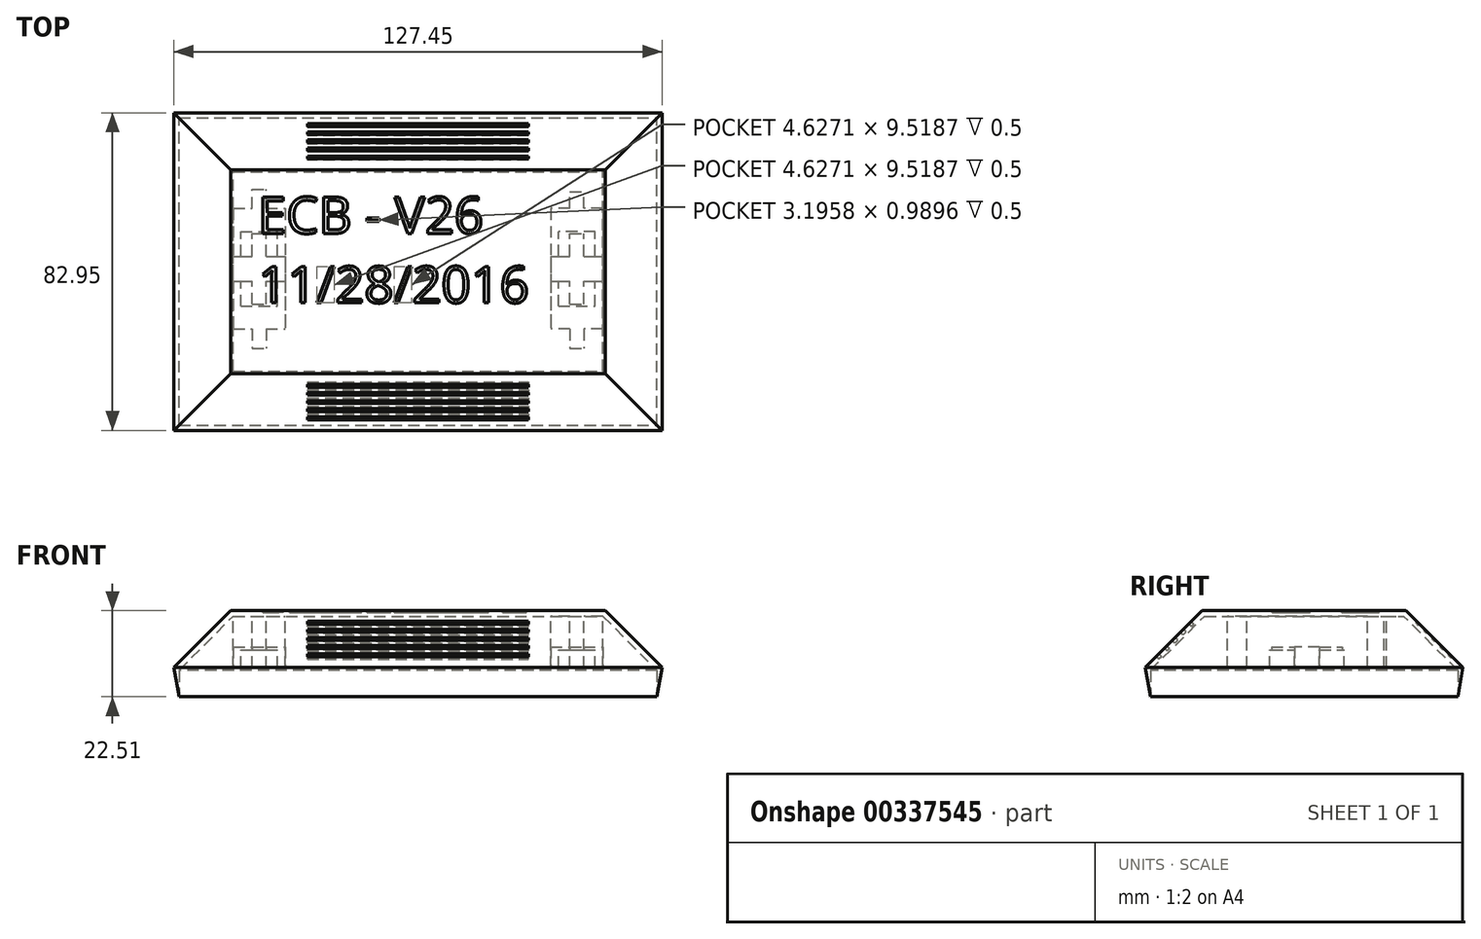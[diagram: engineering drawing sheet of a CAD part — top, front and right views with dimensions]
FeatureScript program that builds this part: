
annotation { "Feature Type Name" : "Feature", "Feature Type Description" : "" }
export const myFeature = defineFeature(function(context is Context, id is Id, definition is map)
    precondition{}
    {
        {
            var Q0;
            Q0=qCreatedBy(makeId("Top.planeOp"),FACE);
            var sketch = newSketch(context, id + "F0", { "sketchPlane" : qUnion([Q0])});
            skLineSegment(sketch, "E0.bottom", {"start": v(0, 0) * mm, "end": v(127.75, 0) * mm});
            skLineSegment(sketch, "E0.top", {"start": v(0, 83.25) * mm, "end": v(127.75, 83.25) * mm});
            skLineSegment(sketch, "E0.left", {"start": v(0, 0) * mm, "end": v(0, 83.25) * mm});
            skLineSegment(sketch, "E0.right", {"start": v(127.75, 0) * mm, "end": v(127.75, 83.25) * mm});
            skLineSegment(sketch, "E1.bottom", {"start": v(0, 0) * mm, "end": v(1.5, 0) * mm});
            skLineSegment(sketch, "E1.left", {"start": v(0, 0) * mm, "end": v(0, 1.5) * mm});
            skLineSegment(sketch, "E2.bottom", {"start": v(127.75, 83.25) * mm, "end": v(126.25, 83.25) * mm});
            skLineSegment(sketch, "E2.left", {"start": v(127.75, 83.25) * mm, "end": v(127.75, 81.75) * mm});
            skSolve(sketch);
        }
        {
            var Q0;
            Q0=makeQuery(id+"F0.imprint","IMPRINT",FACE,{"disambiguationData":[TD([[makeQuery(id+"F0.imprint","IMPRINT",EDGE,{"derivedFrom":sQuery(id+"F0.wireOp",EDGE,"E0.top")}),-1.0]])]});
            var Q1;
            Q1=makeQuery(id+"F0.imprint","IMPRINT",FACE,{"disambiguationData":[TD([[makeQuery(id+"F0.imprint","IMPRINT",EDGE,{"derivedFrom":sQuery(id+"F0.wireOp",EDGE,"E1.bottom")}),1.0]])]});
            var Q2;
            Q2=makeQuery(id+"F0.imprint","IMPRINT",FACE,{"disambiguationData":[TD([[makeQuery(id+"F0.imprint","IMPRINT",EDGE,{"derivedFrom":sQuery(id+"F0.wireOp",EDGE,"E0.bottom")}),1.0]])]});
            var Q3;
            Q3=makeQuery(id+"F0.imprint","IMPRINT",FACE,{"disambiguationData":[TD([[makeQuery(id+"F0.imprint","IMPRINT",EDGE,{"derivedFrom":sQuery(id+"F0.wireOp",EDGE,"E2.bottom")}),1.0]])]});
            extrude(context, id + "F1", {"entities" : qUnion([Q0, Q1, Q2, Q3]), "depth" : 25 * mm});
        }
        {
            var Q0;
            Q0=makeQuery(id+"F1.opExtrude","CAP_EDGE",EDGE,{"disambiguationData":[OSD([sQuery(id+"F0.wireOp",EDGE,"E0.bottom"),sQuery(id+"F0.wireOp",EDGE,"E1.bottom")])],"isStart":false});
            var Q1;
            Q1=makeQuery(id+"F1.opExtrude","CAP_EDGE",EDGE,{"disambiguationData":[OSD([sQuery(id+"F0.wireOp",EDGE,"E0.top"),sQuery(id+"F0.wireOp",EDGE,"E2.bottom")])],"isStart":false});
            var Q2;
            Q2=makeQuery(id+"F1.opExtrude","CAP_EDGE",EDGE,{"disambiguationData":[OSD([sQuery(id+"F0.wireOp",EDGE,"E0.right"),sQuery(id+"F0.wireOp",EDGE,"E2.left")])],"isStart":false});
            var Q3;
            Q3=makeQuery(id+"F1.opExtrude","CAP_EDGE",EDGE,{"disambiguationData":[OSD([sQuery(id+"F0.wireOp",EDGE,"E0.left"),sQuery(id+"F0.wireOp",EDGE,"E1.left")])],"isStart":false});
            chamfer(context, id + "F2", {"entities" : qUnion([Q0, Q1, Q2, Q3]), "width" : 15 * mm, "tangentPropagation" : true});
        }
        {
            var Q0;
            Q0=makeQuery(id+"F1.opExtrude","CAP_FACE",FACE,{"disambiguationData":[OSD([sQuery(id+"F0.wireOp",EDGE,"E0.bottom"),sQuery(id+"F0.wireOp",EDGE,"E0.top"),sQuery(id+"F0.wireOp",EDGE,"E0.left"),sQuery(id+"F0.wireOp",EDGE,"E0.right"),sQuery(id+"F0.wireOp",EDGE,"E1.bottom"),sQuery(id+"F0.wireOp",EDGE,"E1.left"),sQuery(id+"F0.wireOp",EDGE,"E2.bottom"),sQuery(id+"F0.wireOp",EDGE,"E2.left")])],"isStart":true});
            shell(context, id + "F3", {"entities" : qUnion([Q0]), "thickness" : 1.5 * mm});
        }
        {
            var Q0;
            Q0=makeQuery(id+"F1.opExtrude","CAP_EDGE",EDGE,{"disambiguationData":[OSD([sQuery(id+"F0.wireOp",EDGE,"E0.bottom"),sQuery(id+"F0.wireOp",EDGE,"E1.bottom")])],"isStart":true});
            var Q1;
            Q1=makeQuery(id+"F1.opExtrude","CAP_EDGE",EDGE,{"disambiguationData":[OSD([sQuery(id+"F0.wireOp",EDGE,"E0.left"),sQuery(id+"F0.wireOp",EDGE,"E1.left")])],"isStart":true});
            var Q2;
            Q2=makeQuery(id+"F1.opExtrude","CAP_EDGE",EDGE,{"disambiguationData":[OSD([sQuery(id+"F0.wireOp",EDGE,"E0.top"),sQuery(id+"F0.wireOp",EDGE,"E2.bottom")])],"isStart":true});
            var Q3;
            Q3=makeQuery(id+"F1.opExtrude","CAP_EDGE",EDGE,{"disambiguationData":[OSD([sQuery(id+"F0.wireOp",EDGE,"E0.right"),sQuery(id+"F0.wireOp",EDGE,"E2.left")])],"isStart":true});
            chamfer(context, id + "F4", {"entities" : qUnion([Q0, Q1, Q2, Q3]), "chamferType" : ChamferType.OFFSET_ANGLE, "width" : 11 * mm, "oppositeDirection" : false, "angle" : 10 * degree});
        }
        {
            var Q0;
            Q0=makeQuery(id+"F1.opExtrude","CAP_FACE",FACE,{"disambiguationData":[OSD([sQuery(id+"F0.wireOp",EDGE,"E0.bottom"),sQuery(id+"F0.wireOp",EDGE,"E0.top"),sQuery(id+"F0.wireOp",EDGE,"E0.left"),sQuery(id+"F0.wireOp",EDGE,"E0.right"),sQuery(id+"F0.wireOp",EDGE,"E1.bottom"),sQuery(id+"F0.wireOp",EDGE,"E1.left"),sQuery(id+"F0.wireOp",EDGE,"E2.bottom"),sQuery(id+"F0.wireOp",EDGE,"E2.left")])],"isStart":false});
            cPlane(context, id + "F5", {"entities" : qUnion([Q0]), "cplaneType" : CPlaneType.OFFSET, "offset" : 14 * mm, "oppositeDirection" : true, "width" : 150 * mm, "height" : 150 * mm});
        }
        {
            var Q0;
            Q0=makeQuery(id+"F3.opShell","OFFSET_FACE",FACE,{"disambiguationData":[OSD([sQuery(id+"F0.wireOp",EDGE,"E0.bottom"),sQuery(id+"F0.wireOp",EDGE,"E0.top"),sQuery(id+"F0.wireOp",EDGE,"E0.left"),sQuery(id+"F0.wireOp",EDGE,"E0.right"),sQuery(id+"F0.wireOp",EDGE,"E1.bottom"),sQuery(id+"F0.wireOp",EDGE,"E1.left"),sQuery(id+"F0.wireOp",EDGE,"E2.bottom"),sQuery(id+"F0.wireOp",EDGE,"E2.left")])]});
            cPlane(context, id + "F6", {"entities" : qUnion([Q0]), "cplaneType" : CPlaneType.OFFSET, "offset" : 20 * mm, "width" : 150 * mm, "height" : 150 * mm});
        }
        {
            var Q0;
            Q0=makeQuery(id+"F1.opExtrude","CAP_FACE",FACE,{"disambiguationData":[OSD([sQuery(id+"F0.wireOp",EDGE,"E0.bottom"),sQuery(id+"F0.wireOp",EDGE,"E0.top"),sQuery(id+"F0.wireOp",EDGE,"E0.left"),sQuery(id+"F0.wireOp",EDGE,"E0.right"),sQuery(id+"F0.wireOp",EDGE,"E1.bottom"),sQuery(id+"F0.wireOp",EDGE,"E1.left"),sQuery(id+"F0.wireOp",EDGE,"E2.bottom"),sQuery(id+"F0.wireOp",EDGE,"E2.left")])],"isStart":false});
            var sketch = newSketch(context, id + "F7", { "sketchPlane" : qUnion([Q0])});
            skLineSegment(sketch, "E3.bottom", {"start": v(17.62, 32.62) * mm, "end": v(27.22, 32.62) * mm});
            skLineSegment(sketch, "E3.top", {"start": v(17.62, 52.12) * mm, "end": v(27.22, 52.12) * mm});
            skLineSegment(sketch, "E3.left", {"start": v(17.62, 32.62) * mm, "end": v(17.62, 52.12) * mm});
            skLineSegment(sketch, "E3.right", {"start": v(27.22, 32.62) * mm, "end": v(27.22, 52.12) * mm});
            skLineSegment(sketch, "E4", {"start": v(63.87, -44.18) * mm, "end": v(63.87, 54.3) * mm});
            skLineSegment(sketch, "E5.MirrorCS", {"start": v(100.53, 32.62) * mm, "end": v(100.53, 52.12) * mm});
            skLineSegment(sketch, "E6.MirrorCS", {"start": v(110.13, 32.62) * mm, "end": v(100.53, 32.62) * mm});
            skLineSegment(sketch, "E7.MirrorCS", {"start": v(110.13, 32.62) * mm, "end": v(110.13, 52.12) * mm});
            skLineSegment(sketch, "E8.MirrorCS", {"start": v(110.13, 52.12) * mm, "end": v(100.53, 52.12) * mm});
            skLineSegment(sketch, "E9.bottom", {"start": v(15.62, 58.12) * mm, "end": v(29.22, 58.12) * mm});
            skLineSegment(sketch, "E9.top", {"start": v(15.62, 26.62) * mm, "end": v(29.22, 26.62) * mm});
            skLineSegment(sketch, "E9.left", {"start": v(15.62, 58.12) * mm, "end": v(15.62, 26.62) * mm});
            skLineSegment(sketch, "E9.right", {"start": v(29.22, 58.12) * mm, "end": v(29.22, 26.62) * mm});
            skLineSegment(sketch, "E10.MirrorCS", {"start": v(98.53, 58.12) * mm, "end": v(98.53, 26.62) * mm});
            skLineSegment(sketch, "E11.MirrorCS", {"start": v(112.13, 26.62) * mm, "end": v(98.53, 26.62) * mm});
            skLineSegment(sketch, "E12.MirrorCS", {"start": v(112.13, 58.12) * mm, "end": v(112.13, 26.62) * mm});
            skLineSegment(sketch, "E13.MirrorCS", {"start": v(112.13, 58.12) * mm, "end": v(98.53, 58.12) * mm});
            skLineSegment(sketch, "E14.bottom", {"start": v(20.62, 26.62) * mm, "end": v(24.22, 26.62) * mm});
            skLineSegment(sketch, "E14.top", {"start": v(20.62, 21.62) * mm, "end": v(24.22, 21.62) * mm});
            skLineSegment(sketch, "E14.left", {"start": v(20.62, 26.62) * mm, "end": v(20.62, 21.62) * mm});
            skLineSegment(sketch, "E14.right", {"start": v(24.22, 26.62) * mm, "end": v(24.22, 21.62) * mm});
            skLineSegment(sketch, "E15.bottom", {"start": v(20.62, 58.12) * mm, "end": v(24.22, 58.12) * mm});
            skLineSegment(sketch, "E15.top", {"start": v(20.62, 63.12) * mm, "end": v(24.22, 63.12) * mm});
            skLineSegment(sketch, "E15.left", {"start": v(20.62, 58.12) * mm, "end": v(20.62, 63.12) * mm});
            skLineSegment(sketch, "E15.right", {"start": v(24.22, 58.12) * mm, "end": v(24.22, 63.12) * mm});
            skLineSegment(sketch, "E16.bottom", {"start": v(103.53, 26.62) * mm, "end": v(107.13, 26.62) * mm});
            skLineSegment(sketch, "E16.top", {"start": v(103.53, 21.62) * mm, "end": v(107.13, 21.62) * mm});
            skLineSegment(sketch, "E16.left", {"start": v(103.53, 26.62) * mm, "end": v(103.53, 21.62) * mm});
            skLineSegment(sketch, "E16.right", {"start": v(107.13, 26.62) * mm, "end": v(107.13, 21.62) * mm});
            skLineSegment(sketch, "E17.bottom", {"start": v(103.53, 58.12) * mm, "end": v(107.13, 58.12) * mm});
            skLineSegment(sketch, "E17.top", {"start": v(103.53, 62.5) * mm, "end": v(107.13, 62.5) * mm});
            skLineSegment(sketch, "E17.left", {"start": v(103.53, 58.12) * mm, "end": v(103.53, 62.5) * mm});
            skLineSegment(sketch, "E17.right", {"start": v(107.13, 58.12) * mm, "end": v(107.13, 62.5) * mm});
            skSolve(sketch);
        }
        {
            var Q0;
            Q0=qSketchRegion(id+"F7",true);
            extrude(context, id + "F8", {"entities" : qUnion([Q0]), "operationType" : NewBodyOperationType.ADD, "oppositeDirection" : true, "depth" : 15 * mm});
        }
        {
            var Q0;
            {var subQ0=sQuery(id+"F0.wireOp",EDGE,"E1.bottom");var subQ1=sQuery(id+"F0.wireOp",EDGE,"E0.bottom");var subQ2=sQuery(id+"F0.wireOp",EDGE,"E2.bottom");var subQ3=sQuery(id+"F0.wireOp",EDGE,"E0.top");var subQ4=sQuery(id+"F0.wireOp",EDGE,"E1.left");var subQ5=sQuery(id+"F0.wireOp",EDGE,"E0.left");var subQ6=sQuery(id+"F0.wireOp",EDGE,"E2.left");var subQ7=sQuery(id+"F0.wireOp",EDGE,"E0.right");Q0=makeQuery(id+"F8.boolean.opBoolean","SPLIT",FACE,{"disambiguationData":[TD([makeQuery(id+"F8.opExtrude","SWEPT_FACE",FACE,{"disambiguationData":[OSD([sQuery(id+"F7.wireOp",EDGE,"E9.bottom")])]})])],"derivedFrom":makeQuery(id+"F3.opShell","OFFSET_FACE",FACE,{"disambiguationData":[OSD([subQ1,subQ3,subQ5,subQ7,subQ0,subQ4,subQ2,subQ6])]})});}
            cPlane(context, id + "F9", {"entities" : qUnion([Q0]), "cplaneType" : CPlaneType.OFFSET, "offset" : 0 * mm, "width" : 150 * mm, "height" : 150 * mm});
        }
        {
            var Q0;
            Q0=qCreatedBy(id+"F9.planeOp",FACE);
            var sketch = newSketch(context, id + "F10", { "sketchPlane" : qUnion([Q0])});
            skLineSegment(sketch, "E18.bottom", {"start": v(17.62, -32.62) * mm, "end": v(27.22, -32.62) * mm});
            skLineSegment(sketch, "E18.top", {"start": v(17.62, -52.12) * mm, "end": v(27.22, -52.12) * mm});
            skLineSegment(sketch, "E18.left", {"start": v(17.62, -32.62) * mm, "end": v(17.62, -52.12) * mm});
            skLineSegment(sketch, "E18.right", {"start": v(27.22, -32.62) * mm, "end": v(27.22, -52.12) * mm});
            skLineSegment(sketch, "E19.bottom", {"start": v(100.53, -32.62) * mm, "end": v(110.13, -32.62) * mm});
            skLineSegment(sketch, "E19.top", {"start": v(100.53, -52.12) * mm, "end": v(110.13, -52.12) * mm});
            skLineSegment(sketch, "E19.left", {"start": v(100.53, -32.62) * mm, "end": v(100.53, -52.12) * mm});
            skLineSegment(sketch, "E19.right", {"start": v(110.13, -32.62) * mm, "end": v(110.13, -52.12) * mm});
            skSolve(sketch);
        }
        {
            var Q0;
            Q0=qSketchRegion(id+"F10",true);
            extrude(context, id + "F11", {"entities" : qUnion([Q0]), "operationType" : NewBodyOperationType.ADD, "depth" : 8.75 * mm});
        }
        {
            var Q0;
            Q0=makeQuery(id+"F8.opExtrude","CAP_FACE",FACE,{"disambiguationData":[OSD([sQuery(id+"F7.wireOp",EDGE,"E3.bottom"),sQuery(id+"F7.wireOp",EDGE,"E3.top"),sQuery(id+"F7.wireOp",EDGE,"E3.left"),sQuery(id+"F7.wireOp",EDGE,"E3.right"),sQuery(id+"F7.wireOp",EDGE,"E9.bottom"),sQuery(id+"F7.wireOp",EDGE,"E9.top"),sQuery(id+"F7.wireOp",EDGE,"E9.left"),sQuery(id+"F7.wireOp",EDGE,"E9.right")])],"isStart":false});
            cPlane(context, id + "F12", {"entities" : qUnion([Q0]), "cplaneType" : CPlaneType.OFFSET, "offset" : 0 * mm, "width" : 150 * mm, "height" : 150 * mm});
        }
        {
            var Q0;
            Q0=qCreatedBy(id+"F12.planeOp",FACE);
            var sketch = newSketch(context, id + "F13", { "sketchPlane" : qUnion([Q0])});
            skLineSegment(sketch, "E20.bottom", {"start": v(15.62, -45.62) * mm, "end": v(112.13, -45.62) * mm});
            skLineSegment(sketch, "E20.top", {"start": v(15.62, -39.12) * mm, "end": v(112.13, -39.12) * mm});
            skLineSegment(sketch, "E20.left", {"start": v(15.62, -39.12) * mm, "end": v(15.62, -45.62) * mm});
            skLineSegment(sketch, "E20.right", {"start": v(112.13, -39.12) * mm, "end": v(112.13, -45.62) * mm});
            skLineSegment(sketch, "E21.bottom", {"start": v(20.62, -33.12) * mm, "end": v(24.22, -33.12) * mm});
            skLineSegment(sketch, "E21.top", {"start": v(20.62, -51.62) * mm, "end": v(24.22, -51.62) * mm});
            skLineSegment(sketch, "E21.left", {"start": v(20.62, -33.12) * mm, "end": v(20.62, -51.62) * mm});
            skLineSegment(sketch, "E21.right", {"start": v(24.22, -33.12) * mm, "end": v(24.22, -51.62) * mm});
            skLineSegment(sketch, "E22.bottom", {"start": v(103.53, -33.12) * mm, "end": v(107.13, -33.12) * mm});
            skLineSegment(sketch, "E22.top", {"start": v(103.53, -51.62) * mm, "end": v(107.13, -51.62) * mm});
            skLineSegment(sketch, "E22.left", {"start": v(103.53, -33.12) * mm, "end": v(103.53, -51.62) * mm});
            skLineSegment(sketch, "E22.right", {"start": v(107.13, -33.12) * mm, "end": v(107.13, -51.62) * mm});
            skSolve(sketch);
        }
        {
            var Q0;
            Q0=qSketchRegion(id+"F13",true);
            extrude(context, id + "F14", {"entities" : qUnion([Q0]), "operationType" : NewBodyOperationType.REMOVE, "oppositeDirection" : true, "depth" : 5.5 * mm});
        }
        {
            var Q0;
            Q0=makeQuery(id+"F2.opChamfer","BLEND_FACE",FACE,{"disambiguationData":[OSD([sQuery(id+"F0.wireOp",EDGE,"E0.bottom"),sQuery(id+"F0.wireOp",EDGE,"E1.bottom")])]});
            var sketch = newSketch(context, id + "F15", { "sketchPlane" : qUnion([Q0])});
            skLineSegment(sketch, "E23.bottom", {"start": v(35, 21.28) * mm, "end": v(92.75, 21.28) * mm});
            skLineSegment(sketch, "E23.top", {"start": v(35, 20.28) * mm, "end": v(92.75, 20.28) * mm});
            skLineSegment(sketch, "E23.left", {"start": v(35, 21.28) * mm, "end": v(35, 20.28) * mm});
            skLineSegment(sketch, "E23.right", {"start": v(92.75, 21.28) * mm, "end": v(92.75, 20.28) * mm});
            skLineSegment(sketch, "E24.MirrorCS", {"start": v(92.75, 17.28) * mm, "end": v(92.75, 18.28) * mm});
            skLineSegment(sketch, "E25.MirrorCS", {"start": v(35, 17.28) * mm, "end": v(35, 18.28) * mm});
            skLineSegment(sketch, "E26.MirrorCS", {"start": v(35, 17.28) * mm, "end": v(92.75, 17.28) * mm});
            skLineSegment(sketch, "E27.MirrorCS", {"start": v(35, 18.28) * mm, "end": v(92.75, 18.28) * mm});
            skLineSegment(sketch, "E28.MirrorCS", {"start": v(92.75, 15.28) * mm, "end": v(92.75, 14.28) * mm});
            skLineSegment(sketch, "E29.MirrorCS", {"start": v(35, 15.28) * mm, "end": v(35, 14.28) * mm});
            skLineSegment(sketch, "E30.MirrorCS", {"start": v(35, 14.28) * mm, "end": v(92.75, 14.28) * mm});
            skLineSegment(sketch, "E31.MirrorCS", {"start": v(35, 15.28) * mm, "end": v(92.75, 15.28) * mm});
            skLineSegment(sketch, "E32.bottom", {"start": v(35, 24.28) * mm, "end": v(92.75, 24.28) * mm});
            skLineSegment(sketch, "E32.top", {"start": v(35, 23.28) * mm, "end": v(92.75, 23.28) * mm});
            skLineSegment(sketch, "E32.left", {"start": v(35, 24.28) * mm, "end": v(35, 23.28) * mm});
            skLineSegment(sketch, "E32.right", {"start": v(92.75, 24.28) * mm, "end": v(92.75, 23.28) * mm});
            skLineSegment(sketch, "E33.MirrorCS", {"start": v(92.75, 12.28) * mm, "end": v(92.75, 11.28) * mm});
            skLineSegment(sketch, "E34.MirrorCS", {"start": v(35, 12.28) * mm, "end": v(35, 11.28) * mm});
            skLineSegment(sketch, "E35.MirrorCS", {"start": v(35, 11.28) * mm, "end": v(92.75, 11.28) * mm});
            skLineSegment(sketch, "E36.MirrorCS", {"start": v(35, 12.28) * mm, "end": v(92.75, 12.28) * mm});
            skSolve(sketch);
        }
        {
            var Q0;
            Q0 = qSketchRegion(id + "F15", true);
            extrude(context, id + "F16", {"entities" : qUnion([Q0]), "operationType" : NewBodyOperationType.REMOVE, "oppositeDirection" : true, "depth" : 1 * mm, "offsetDistance" : 25 * mm});
        }
        {
            var Q0;
            Q0=makeQuery(id+"F2.opChamfer","BLEND_FACE",FACE,{"disambiguationData":[OSD([sQuery(id+"F0.wireOp",EDGE,"E0.top"),sQuery(id+"F0.wireOp",EDGE,"E2.bottom")])]});
            var sketch = newSketch(context, id + "F17", { "sketchPlane" : qUnion([Q0])});
            skLineSegment(sketch, "E37.bottom", {"start": v(-92.75, -34.58) * mm, "end": v(-35, -34.58) * mm});
            skLineSegment(sketch, "E37.top", {"start": v(-92.75, -35.58) * mm, "end": v(-35, -35.58) * mm});
            skLineSegment(sketch, "E37.left", {"start": v(-92.75, -34.58) * mm, "end": v(-92.75, -35.58) * mm});
            skLineSegment(sketch, "E37.right", {"start": v(-35, -34.58) * mm, "end": v(-35, -35.58) * mm});
            skLineSegment(sketch, "E38.bottom", {"start": v(-92.75, -37.58) * mm, "end": v(-35, -37.58) * mm});
            skLineSegment(sketch, "E38.top", {"start": v(-92.75, -38.58) * mm, "end": v(-35, -38.58) * mm});
            skLineSegment(sketch, "E38.left", {"start": v(-92.75, -37.58) * mm, "end": v(-92.75, -38.58) * mm});
            skLineSegment(sketch, "E38.right", {"start": v(-35, -37.58) * mm, "end": v(-35, -38.58) * mm});
            skLineSegment(sketch, "E39.bottom", {"start": v(-92.75, -40.58) * mm, "end": v(-35, -40.58) * mm});
            skLineSegment(sketch, "E39.top", {"start": v(-92.75, -41.58) * mm, "end": v(-35, -41.58) * mm});
            skLineSegment(sketch, "E39.left", {"start": v(-92.75, -40.58) * mm, "end": v(-92.75, -41.58) * mm});
            skLineSegment(sketch, "E39.right", {"start": v(-35, -40.58) * mm, "end": v(-35, -41.58) * mm});
            skLineSegment(sketch, "E40.bottom", {"start": v(-92.75, -43.58) * mm, "end": v(-35, -43.58) * mm});
            skLineSegment(sketch, "E40.top", {"start": v(-92.75, -44.58) * mm, "end": v(-35, -44.58) * mm});
            skLineSegment(sketch, "E40.left", {"start": v(-92.75, -43.58) * mm, "end": v(-92.75, -44.58) * mm});
            skLineSegment(sketch, "E40.right", {"start": v(-35, -43.58) * mm, "end": v(-35, -44.58) * mm});
            skLineSegment(sketch, "E41.bottom", {"start": v(-92.75, -46.58) * mm, "end": v(-35, -46.58) * mm});
            skLineSegment(sketch, "E41.top", {"start": v(-92.75, -47.58) * mm, "end": v(-35, -47.58) * mm});
            skLineSegment(sketch, "E41.left", {"start": v(-92.75, -46.58) * mm, "end": v(-92.75, -47.58) * mm});
            skLineSegment(sketch, "E41.right", {"start": v(-35, -46.58) * mm, "end": v(-35, -47.58) * mm});
            skSolve(sketch);
        }
        {
            var Q0;
            Q0 = qSketchRegion(id + "F17", true);
            extrude(context, id + "F18", {"entities" : qUnion([Q0]), "operationType" : NewBodyOperationType.REMOVE, "oppositeDirection" : true, "depth" : 0.5 * mm});
        }
        {
            var Q0;
            Q0=makeQuery(id+"F1.opExtrude","CAP_FACE",FACE,{"disambiguationData":[OSD([sQuery(id+"F0.wireOp",EDGE,"E0.bottom"),sQuery(id+"F0.wireOp",EDGE,"E0.top"),sQuery(id+"F0.wireOp",EDGE,"E0.left"),sQuery(id+"F0.wireOp",EDGE,"E0.right"),sQuery(id+"F0.wireOp",EDGE,"E1.bottom"),sQuery(id+"F0.wireOp",EDGE,"E1.left"),sQuery(id+"F0.wireOp",EDGE,"E2.bottom"),sQuery(id+"F0.wireOp",EDGE,"E2.left")])],"isStart":false});
            var sketch = newSketch(context, id + "F19", { "sketchPlane" : qUnion([Q0])});
            skText(sketch, "E42", { "text": "ECB - V26\n11/28/2016", "fontName": "OpenSans-Regular.ttf"});
            const initialGuessF19  = {"E42": [0.02209, 0.0516, 1, 0, 0.0096]};
            skSetInitialGuess(sketch, initialGuessF19);
            skSolve(sketch);
        }
        {
            var Q0;
            Q0 = qSketchRegion(id + "F19", true);
            extrude(context, id + "F20", {"entities" : qUnion([Q0]), "operationType" : NewBodyOperationType.REMOVE, "oppositeDirection" : true, "depth" : 0.5 * mm});
        }
    });
